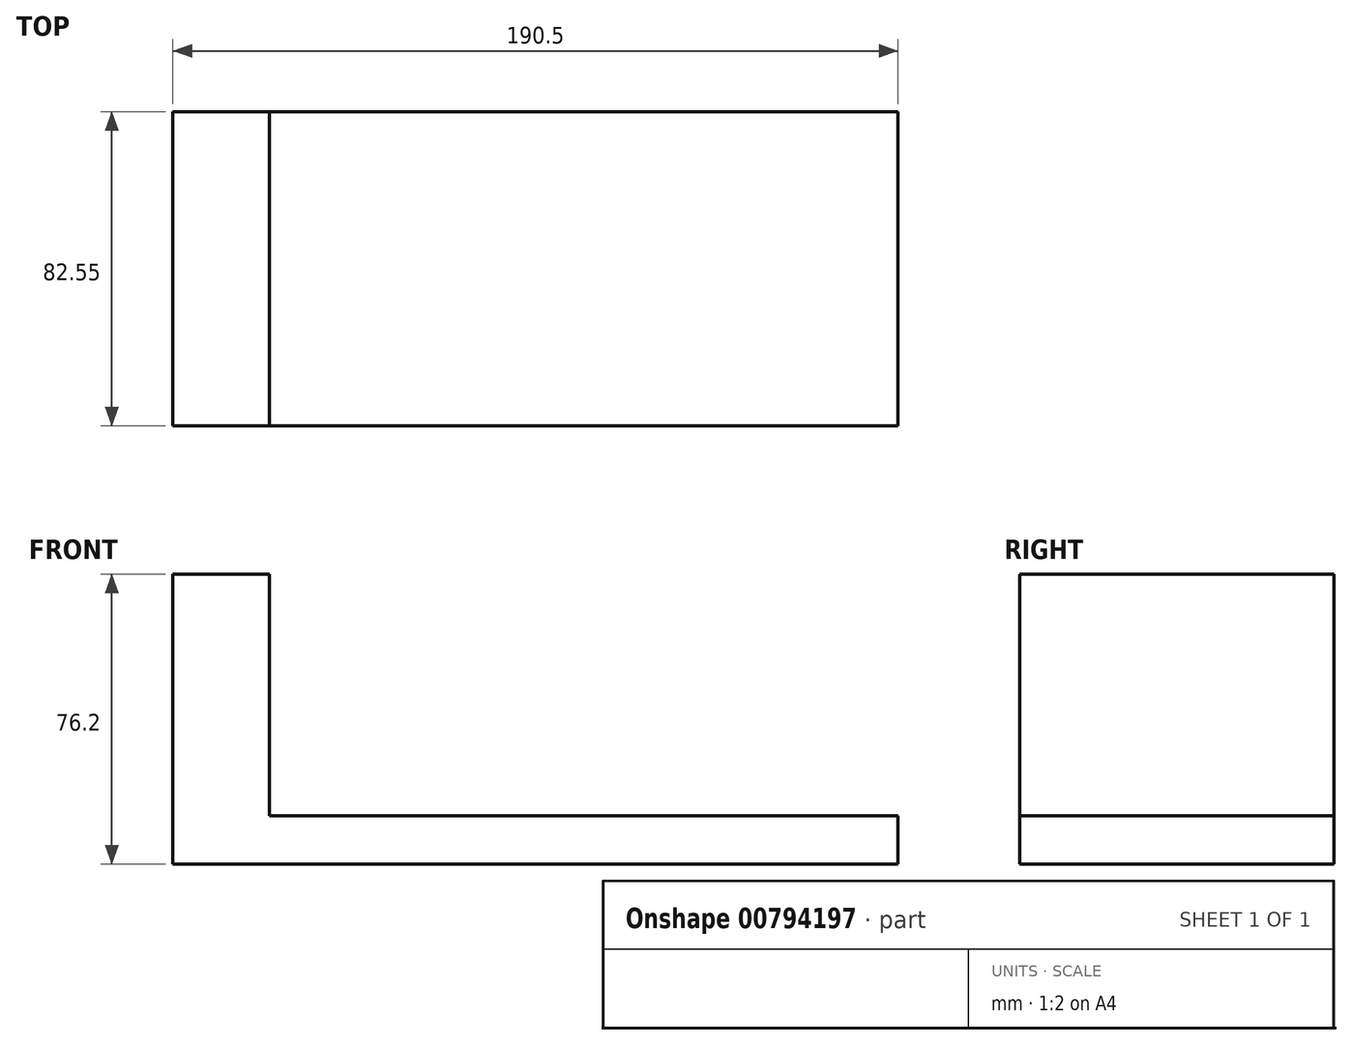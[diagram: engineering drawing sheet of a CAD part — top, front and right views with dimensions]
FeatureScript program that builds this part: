
annotation { "Feature Type Name" : "Feature", "Feature Type Description" : "" }
export const myFeature = defineFeature(function(context is Context, id is Id, definition is map)
    precondition{}
    {
        {
            var Q0;
            Q0=qCreatedBy(makeId("Front.planeOp"),FACE);
            var sketch = newSketch(context, id + "F0", { "sketchPlane" : qUnion([Q0])});
            skLineSegment(sketch, "E0", {"start": v(0, 0) * mm, "end": v(190.5, 0) * mm});
            skLineSegment(sketch, "E1", {"start": v(0, 0) * mm, "end": v(0, 76.2) * mm});
            skLineSegment(sketch, "E2", {"start": v(0, 76.2) * mm, "end": v(190.5, 76.2) * mm});
            skLineSegment(sketch, "E3", {"start": v(190.5, 76.2) * mm, "end": v(190.5, 0) * mm});
            skSolve(sketch);
        }
        {
            var Q0;
            Q0 = qSketchRegion(id + "F0", true);
            extrude(context, id + "F1", {"entities" : qUnion([Q0]), "depth" : 82.55 * mm, "offsetDistance" : 25.4 * mm});
        }
        {
            var Q0;
            Q0=makeQuery(id+"F1.opExtrude","CAP_FACE",FACE,{"disambiguationData":[OSD([sQuery(id+"F0.wireOp",EDGE,"E0"),sQuery(id+"F0.wireOp",EDGE,"E1"),sQuery(id+"F0.wireOp",EDGE,"E2"),sQuery(id+"F0.wireOp",EDGE,"E3")])],"isStart":false});
            var sketch = newSketch(context, id + "F2", { "sketchPlane" : qUnion([Q0])});
            skLineSegment(sketch, "E4", {"start": v(0, 0) * mm, "end": v(25.4, 0) * mm});
            skLineSegment(sketch, "E5", {"start": v(25.4, 0) * mm, "end": v(25.4, 12.7) * mm});
            skLineSegment(sketch, "E6", {"start": v(25.4, 12.7) * mm, "end": v(25.4, 76.2) * mm});
            skLineSegment(sketch, "E7", {"start": v(25.4, 76.2) * mm, "end": v(190.5, 76.2) * mm});
            skLineSegment(sketch, "E8", {"start": v(190.5, 76.2) * mm, "end": v(190.5, 12.7) * mm});
            skLineSegment(sketch, "E9", {"start": v(190.5, 12.7) * mm, "end": v(25.4, 12.7) * mm});
            skSolve(sketch);
        }
        {
            var Q0;
            Q0=makeQuery(id+"F2.imprint","IMPRINT",FACE,{"disambiguationData":[TD([[makeQuery(id+"F2.imprint","IMPRINT",EDGE,{"derivedFrom":sQuery(id+"F2.wireOp",EDGE,"E6")}),-1.0]])]});
            extrude(context, id + "F3", {"entities" : qUnion([Q0]), "operationType" : NewBodyOperationType.REMOVE, "oppositeDirection" : true, "depth" : 82.55 * mm, "offsetDistance" : 25.4 * mm});
        }
    });
